# Revit family: Hager-FW-IP30-With_Door-With_notch-syst-NoHosted-CH-en
name_source: partatom
category: Electrical Equipment
units: mm (PartAtom-declared; Revit-internal decimal feet)

## family parameters
Always vertical = Yes
Cut with Voids When Loaded = No
Panel Configuration = Two Columns, Circuits Across
Part Type = Panelboard
Room Calculation Point = No
Round Connector Dimension = Use Diameter
Shared = No
Work Plane-Based = Yes

## types (20) — shared parameters
Default Elevation = 1219 mm
EF000003 - Mounting method = EV000128 - Hollow wall
EF000007 - Colour = EV000202 - White
EF000049 - Depth = 125 mm  [stored 0.410105 ft]
EF000116 - RAL-number = 9010
EF000218 - Built-in depth = 112 mm  [stored 0.367454 ft]
EF000339 - Type of cover = EV004216 - Door
EF001062 - EMC-version = No
EF001088 - Extension possible = Yes
EF001131 - Internal depth = 112 mm  [stored 0.367454 ft]
EF001134 - DIN-rail = Yes
EF001596 - Material housing = EV000179 - Steel
EF002950 - Width in number of modular spacings = 12
EF004462 - Type of closure = EV000154 - Other
EF005474 - Degree of protection (IP) = EV006410 - IP30
EF006244 - Transparent cover/door = No
EF006306 - With lock = No
EF009212 - Cover model = EV009916 - With notch
EF015776 - Earthing terminal block = No
EF015777 - Neutral terminal block = No
EF015941 - Signal passing door = No
HG000002 - With door or cover = Yes
HG000003 - Range = FW
HG000005 - Thickness = 3 mm  [stored 0.00984252 ft]
HG000006 - Flush mounted = Yes
HG000011 - Empty rows from bottom = No
HG000017 - Distance between poles = 18 mm  [stored 0.0590551 ft]
Manufacturer = Hager
Type Comments = FW

## per-type parameters (varying)
| type | EF000008 - Width | EF000040 - Height | EF000118 - With mounting plate | EF000266 - Number of rows | EF000332 - Built-in height | EF000846 - Built-in width | HG000001 - Number of columns | HG000004 - Manufacturer reference | HG000007 - Number of empty columns | HG000008 - Number of empty rows | HG000009 - Double swing door | HG000010 - Asymmetric doors | Model |
| Recessed mounted IP30 W353 H1003 D125 12 Modular spacings - FWU61S1 | 353 mm  [stored 1.15814 ft] | 1003 mm  [stored 3.29068 ft] | No | 6 | 952 mm  [stored 3.12336 ft] | 310 mm  [stored 1.01706 ft] | 1 | FWU61S1 | 0 | 0 | No | No | FWU61S1 |
| Recessed mounted IP30 W353 H1153 D125 12 Modular spacings - FWU71S1 | 353 mm  [stored 1.15814 ft] | 1153 mm | No | 7 | 1102 mm  [stored 3.61549 ft] | 310 mm  [stored 1.01706 ft] | 1 | FWU71S1 | 0 | 0 | No | No | FWU71S1 |
| Recessed mounted IP30 W353 H553 D125 12 Modular spacings - FWU31S1 | 353 mm  [stored 1.15814 ft] | 553 mm  [stored 1.8143 ft] | No | 3 | 502 mm  [stored 1.64698 ft] | 310 mm  [stored 1.01706 ft] | 1 | FWU31S1 | 0 | 0 | No | No | FWU31S1 |
| Recessed mounted IP30 W353 H703 D125 12 Modular spacings - FWU41S1 | 353 mm  [stored 1.15814 ft] | 703 mm  [stored 2.30643 ft] | No | 4 | 652 mm  [stored 2.13911 ft] | 310 mm  [stored 1.01706 ft] | 1 | FWU41S1 | 0 | 0 | No | No | FWU41S1 |
| Recessed mounted IP30 W353 H853 D125 12 Modular spacings - FWU51S1 | 353 mm  [stored 1.15814 ft] | 853 mm  [stored 2.79856 ft] | No | 5 | 802 mm  [stored 2.63123 ft] | 310 mm  [stored 1.01706 ft] | 1 | FWU51S1 | 0 | 0 | No | No | FWU51S1 |
| Recessed mounted IP30 W603 H1003 D125 12 Modular spacings - FWU62K | 603 mm | 1003 mm  [stored 3.29068 ft] | Yes | 6 | 952 mm  [stored 3.12336 ft] | 560 mm  [stored 1.83727 ft] | 1 | FWU62K | 1 | 6 | No | No | FWU62K |
| Recessed mounted IP30 W603 H1003 D125 12 Modular spacings - FWU62S1 | 603 mm | 1003 mm  [stored 3.29068 ft] | No | 12 | 952 mm  [stored 3.12336 ft] | 560 mm  [stored 1.83727 ft] | 2 | FWU62S1 | 0 | 0 | No | No | FWU62S1 |
| Recessed mounted IP30 W603 H1153 D125 12 Modular spacings - FWU72S1 | 603 mm | 1153 mm | No | 14 | 1102 mm  [stored 3.61549 ft] | 560 mm  [stored 1.83727 ft] | 2 | FWU72S1 | 0 | 0 | No | No | FWU72S1 |
| Recessed mounted IP30 W603 H553 D125 12 Modular spacings - FWU32S1 | 603 mm | 553 mm  [stored 1.8143 ft] | No | 6 | 502 mm  [stored 1.64698 ft] | 560 mm  [stored 1.83727 ft] | 2 | FWU32S1 | 0 | 0 | No | No | FWU32S1 |
| Recessed mounted IP30 W603 H703 D125 12 Modular spacings - FWU42K | 603 mm | 703 mm  [stored 2.30643 ft] | Yes | 4 | 652 mm  [stored 2.13911 ft] | 560 mm  [stored 1.83727 ft] | 1 | FWU42K | 1 | 4 | No | No | FWU42K |
| Recessed mounted IP30 W603 H703 D125 12 Modular spacings - FWU42S1 | 603 mm | 703 mm  [stored 2.30643 ft] | No | 8 | 652 mm  [stored 2.13911 ft] | 560 mm  [stored 1.83727 ft] | 2 | FWU42S1 | 0 | 0 | No | No | FWU42S1 |
| Recessed mounted IP30 W603 H853 D125 12 Modular spacings - FWU52K | 603 mm | 853 mm  [stored 2.79856 ft] | Yes | 5 | 802 mm  [stored 2.63123 ft] | 560 mm  [stored 1.83727 ft] | 1 | FWU52K | 1 | 5 | No | No | FWU52K |
| Recessed mounted IP30 W603 H853 D125 12 Modular spacings - FWU52S1 | 603 mm | 853 mm  [stored 2.79856 ft] | No | 10 | 802 mm  [stored 2.63123 ft] | 560 mm  [stored 1.83727 ft] | 2 | FWU52S1 | 0 | 0 | No | No | FWU52S1 |
| Recessed mounted IP30 W853 H1003 D125 12 Modular spacings - FWU63S1 | 853 mm  [stored 2.79856 ft] | 1003 mm  [stored 3.29068 ft] | No | 18 | 952 mm  [stored 3.12336 ft] | 810 mm | 3 | FWU63S1 | 0 | 0 | Yes | Yes | FWU63S1 |
| Recessed mounted IP30 W853 H1153 D125 12 Modular spacings - FWU73S1 | 853 mm  [stored 2.79856 ft] | 1153 mm | No | 21 | 1102 mm  [stored 3.61549 ft] | 810 mm | 3 | FWU73S1 | 0 | 0 | Yes | Yes | FWU73S1 |
| Recessed mounted IP30 W853 H553 D125 12 Modular spacings - FWU33S1 | 853 mm  [stored 2.79856 ft] | 553 mm  [stored 1.8143 ft] | No | 9 | 502 mm  [stored 1.64698 ft] | 810 mm | 3 | FWU33S1 | 0 | 0 | Yes | Yes | FWU33S1 |
| Recessed mounted IP30 W853 H703 D125 12 Modular spacings - FWU43K | 853 mm  [stored 2.79856 ft] | 703 mm  [stored 2.30643 ft] | Yes | 8 | 652 mm  [stored 2.13911 ft] | 810 mm | 2 | FWU43K | 1 | 4 | Yes | Yes | FWU43K |
| Recessed mounted IP30 W853 H703 D125 12 Modular spacings - FWU43S1 | 853 mm  [stored 2.79856 ft] | 703 mm  [stored 2.30643 ft] | No | 12 | 652 mm  [stored 2.13911 ft] | 810 mm | 3 | FWU43S1 | 0 | 0 | Yes | Yes | FWU43S1 |
| Recessed mounted IP30 W853 H853 D125 12 Modular spacings - FWU53K | 853 mm  [stored 2.79856 ft] | 853 mm  [stored 2.79856 ft] | Yes | 10 | 802 mm  [stored 2.63123 ft] | 810 mm | 2 | FWU53K | 1 | 5 | Yes | Yes | FWU53K |
| Recessed mounted IP30 W853 H853 D125 12 Modular spacings - FWU53S1 | 853 mm  [stored 2.79856 ft] | 853 mm  [stored 2.79856 ft] | No | 15 | 802 mm  [stored 2.63123 ft] | 810 mm | 3 | FWU53S1 | 0 | 0 | Yes | Yes | FWU53S1 |

note: [stored X ft] marks values corroborated as IEEE doubles in the binary element streams (Revit-internal decimal feet)

## geometry (parser evidence)
native form markers: Sweep x14
no freeform markers — native parametric forms only
